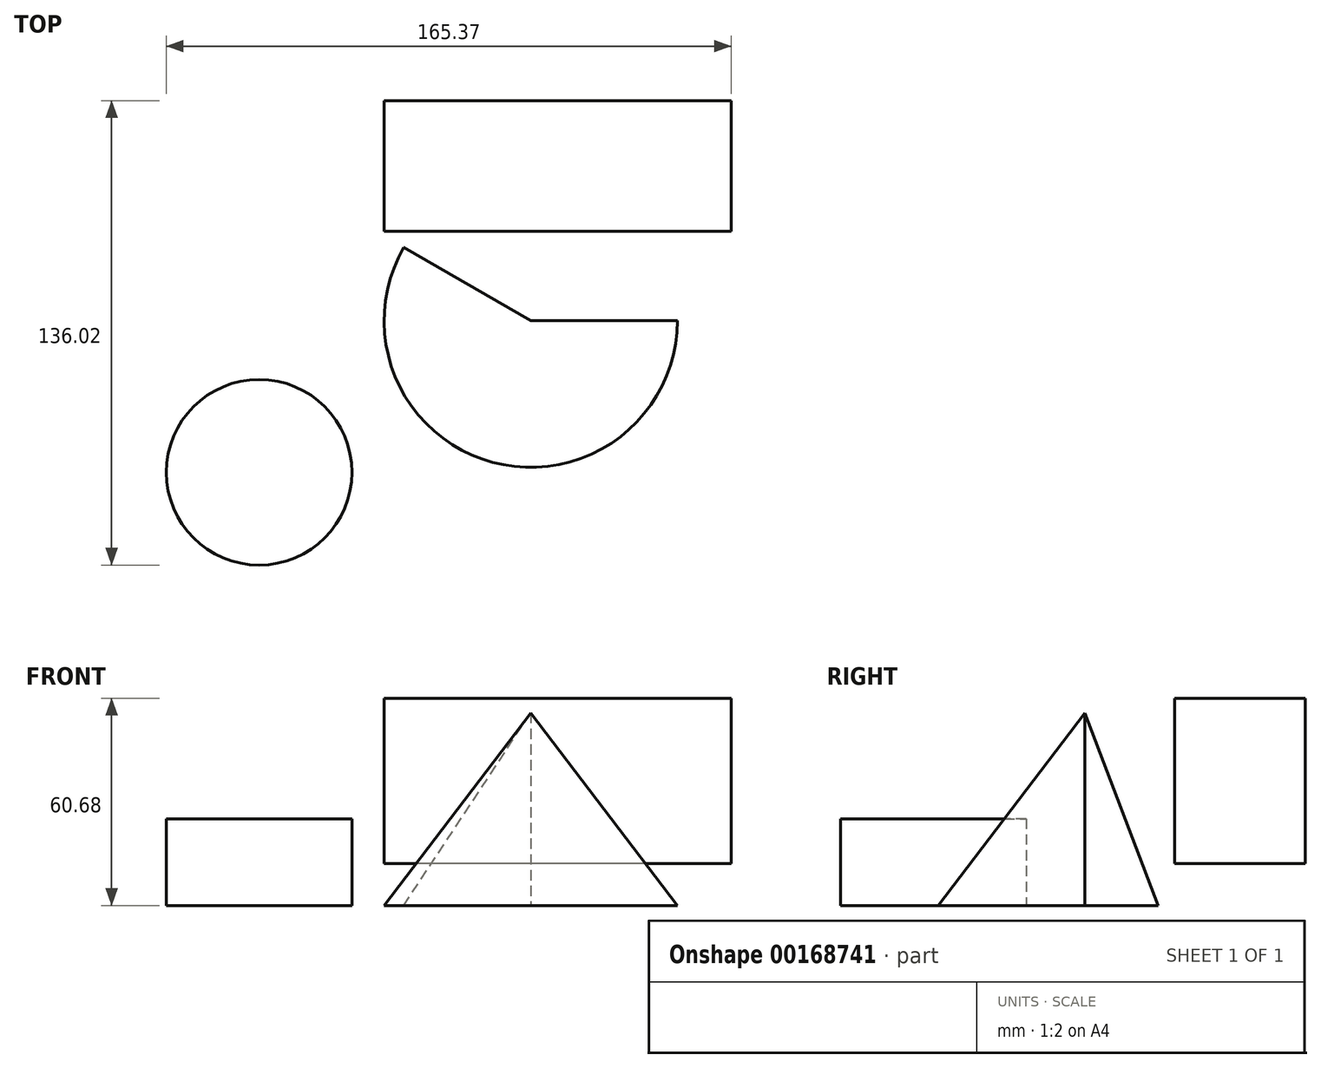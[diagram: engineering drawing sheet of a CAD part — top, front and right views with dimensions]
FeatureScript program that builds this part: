
annotation { "Feature Type Name" : "Feature", "Feature Type Description" : "" }
export const myFeature = defineFeature(function(context is Context, id is Id, definition is map)
    precondition{}
    {
        {
            var Q0;
            Q0=qCreatedBy(makeId("Front.planeOp"),FACE);
            var sketch = newSketch(context, id + "F0", { "sketchPlane" : qUnion([Q0])});
            skLineSegment(sketch, "E0", {"start": v(0, 0) * mm, "end": v(42.91, 56.38) * mm});
            skLineSegment(sketch, "E1", {"start": v(42.91, 56.38) * mm, "end": v(42.91, 0) * mm});
            skLineSegment(sketch, "E2", {"start": v(42.91, 0) * mm, "end": v(0, 0) * mm});
            skSolve(sketch);
        }
        {
            var Q0;
            Q0 = qSketchRegion(id + "F0", true);
            var Q1;
            Q1=sQuery(id+"F0.wireOp",EDGE,"E1");
            revolve(context, id + "F1", {"entities" : qUnion([Q0]), "axis" : qUnion([Q1]), "revolveType" : RevolveType.TWO_DIRECTIONS, "angle" : 30 * degree, "angleBack" : 180 * degree});
        }
        {
            var Q0;
            Q0=qCreatedBy(makeId("Right.planeOp"),FACE);
            var sketch = newSketch(context, id + "F2", { "sketchPlane" : qUnion([Q0])});
            skLineSegment(sketch, "E3.bottom", {"start": v(64.48, 60.68) * mm, "end": v(26.28, 60.68) * mm});
            skLineSegment(sketch, "E3.top", {"start": v(64.48, 12.32) * mm, "end": v(26.28, 12.32) * mm});
            skLineSegment(sketch, "E3.left", {"start": v(64.48, 60.68) * mm, "end": v(64.48, 12.32) * mm});
            skLineSegment(sketch, "E3.right", {"start": v(26.28, 60.68) * mm, "end": v(26.28, 12.32) * mm});
            skSolve(sketch);
        }
        {
            var Q0;
            Q0 = qSketchRegion(id + "F2", true);
            extrude(context, id + "F3", {"entities" : qUnion([Q0]), "depth" : 101.6 * mm});
        }
        {
            var Q0;
            Q0=qCreatedBy(makeId("Top.planeOp"),FACE);
            var sketch = newSketch(context, id + "F4", { "sketchPlane" : qUnion([Q0])});
            skCircle(sketch, "E4", {"center": v(-36.6, -44.36) * mm, "radius": 27.17 * mm});
            skSolve(sketch);
        }
        {
            var Q0;
            Q0 = qSketchRegion(id + "F4", true);
            extrude(context, id + "F5", {"entities" : qUnion([Q0]), "depth" : 25.4 * mm});
        }
    });
